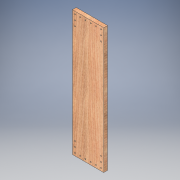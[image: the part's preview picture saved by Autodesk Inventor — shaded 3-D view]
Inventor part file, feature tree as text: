
AUTODESK INVENTOR PART (.ipt)
format: ipt  version: 2018 (Build 220112000, 112)  size: 169,984 bytes
history: native  units: in
note: dims shown in document units (in); Inventor stores cm internally (conversion verified against a paired STEP export)
features: extrude x3, sketch x3
ambient origin geometry x8: Origin, YZ Plane, XZ Plane, XY Plane, X Axis, Y Axis, Z Axis, Center Point
bodies: Solid1 (feature_tree)
feature tree (6):
  extrude  "Extrusion1"  Depth=24.0in
  extrude  "Extrusion2"  Depth=0.75in
  extrude  "Extrusion3"  Depth=0.75in
  sketch  "Sketch1"  dims[d0=6.0in d1=24.0in]
  sketch  "Sketch2"  dims[d2=0.75in d3=0.0in d4=0.5in]
  sketch  "Sketch3"  dims[d5=0.5in d6=0.2031in d7=0.75in d8=0.0in d9=1.0in d10=1.0in d11=1.0in d12=1.0in d13=0.75in d14=0.0in]
